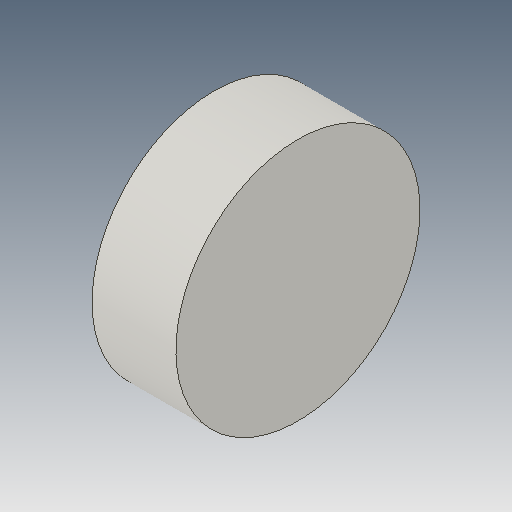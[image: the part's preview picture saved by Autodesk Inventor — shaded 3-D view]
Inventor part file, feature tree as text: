
AUTODESK INVENTOR PART (.ipt)
format: ipt  version: 2018 (Build 220112000, 112)  size: 83,456 bytes
history: native  units: in
note: dims shown in document units (in); Inventor stores cm internally (conversion verified against a paired STEP export)
features: other x3, sketch x1
ambient origin geometry x8: Origin, YZ Plane, XZ Plane, XY Plane, X Axis, Y Axis, Z Axis, Center Point
bodies: Solid1 (feature_tree)
feature tree (4):
  other  "Wheel_MIR.ipt"
  other  "Solid1::Wheel_MIR.ipt"
  other  "TaggingFeature1"
  sketch  "Sketch1"  dims[d0=0.3937in]
